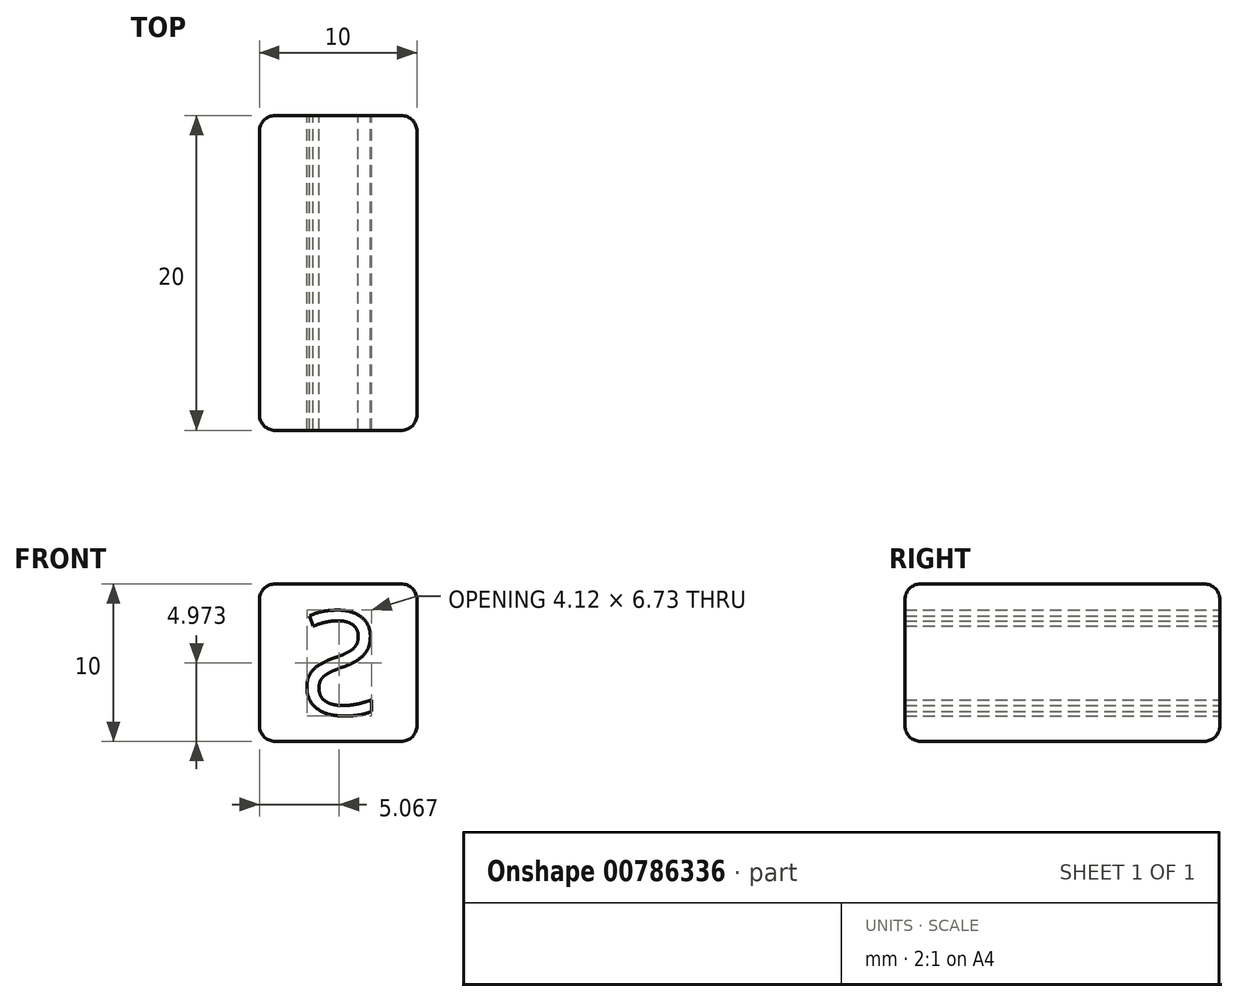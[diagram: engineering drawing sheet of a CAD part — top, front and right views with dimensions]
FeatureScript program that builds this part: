
annotation { "Feature Type Name" : "Feature", "Feature Type Description" : "" }
export const myFeature = defineFeature(function(context is Context, id is Id, definition is map)
    precondition{}
    {
        {
            var Q0;
            Q0=qCreatedBy(makeId("Front.planeOp"),FACE);
            var sketch = newSketch(context, id + "F0", { "sketchPlane" : qUnion([Q0])});
            skLineSegment(sketch, "E0.bottom", {"start": v(0, 0) * mm, "end": v(10, 0) * mm});
            skLineSegment(sketch, "E0.top", {"start": v(0, 10) * mm, "end": v(10, 10) * mm});
            skLineSegment(sketch, "E0.left", {"start": v(0, 0) * mm, "end": v(0, 10) * mm});
            skLineSegment(sketch, "E0.right", {"start": v(10, 0) * mm, "end": v(10, 10) * mm});
            skSolve(sketch);
        }
        {
            var Q0;
            Q0 = qSketchRegion(id + "F0", true);
            extrude(context, id + "F1", {"entities" : qUnion([Q0]), "depth" : 20 * mm, "offsetDistance" : 25 * mm});
        }
        {
            var Q0;
            Q0=makeQuery(id+"F1.opExtrude","SWEPT_FACE",FACE,{"disambiguationData":[OSD([sQuery(id+"F0.wireOp",EDGE,"E0.top")])]});
            var Q1;
            Q1=makeQuery(id+"F1.opExtrude","SWEPT_FACE",FACE,{"disambiguationData":[OSD([sQuery(id+"F0.wireOp",EDGE,"E0.right")])]});
            var Q2;
            Q2=makeQuery(id+"F1.opExtrude","SWEPT_FACE",FACE,{"disambiguationData":[OSD([sQuery(id+"F0.wireOp",EDGE,"E0.bottom")])]});
            var Q3;
            Q3=makeQuery(id+"F1.opExtrude","SWEPT_FACE",FACE,{"disambiguationData":[OSD([sQuery(id+"F0.wireOp",EDGE,"E0.left")])]});
            fillet(context, id + "F2", {"entities" : qUnion([Q0, Q1, Q2, Q3]), "radius" : 1 * mm, "tangentPropagation" : true, "allowEdgeOverflow" : false});
        }
        {
            var Q0;
            Q0=makeQuery(id+"F1.opExtrude","CAP_FACE",FACE,{"disambiguationData":[OSD([sQuery(id+"F0.wireOp",EDGE,"E0.bottom"),sQuery(id+"F0.wireOp",EDGE,"E0.top"),sQuery(id+"F0.wireOp",EDGE,"E0.left"),sQuery(id+"F0.wireOp",EDGE,"E0.right")])],"isStart":true});
            var sketch = newSketch(context, id + "F3", { "sketchPlane" : qUnion([Q0])});
            skText(sketch, "E1", { "text": "S\n", "fontName": "OpenSans-Regular.ttf"});
            const initialGuessF3  = {"E1": [-0.0076, 0.0017, 1, 0, 0.0066]};
            skSetInitialGuess(sketch, initialGuessF3);
            skSolve(sketch);
        }
        {
            var Q0;
            Q0 = qSketchRegion(id + "F3", true);
            extrude(context, id + "F4", {"entities" : qUnion([Q0]), "operationType" : NewBodyOperationType.REMOVE, "oppositeDirection" : true, "depth" : 25 * mm, "offsetDistance" : 25 * mm});
        }
    });
